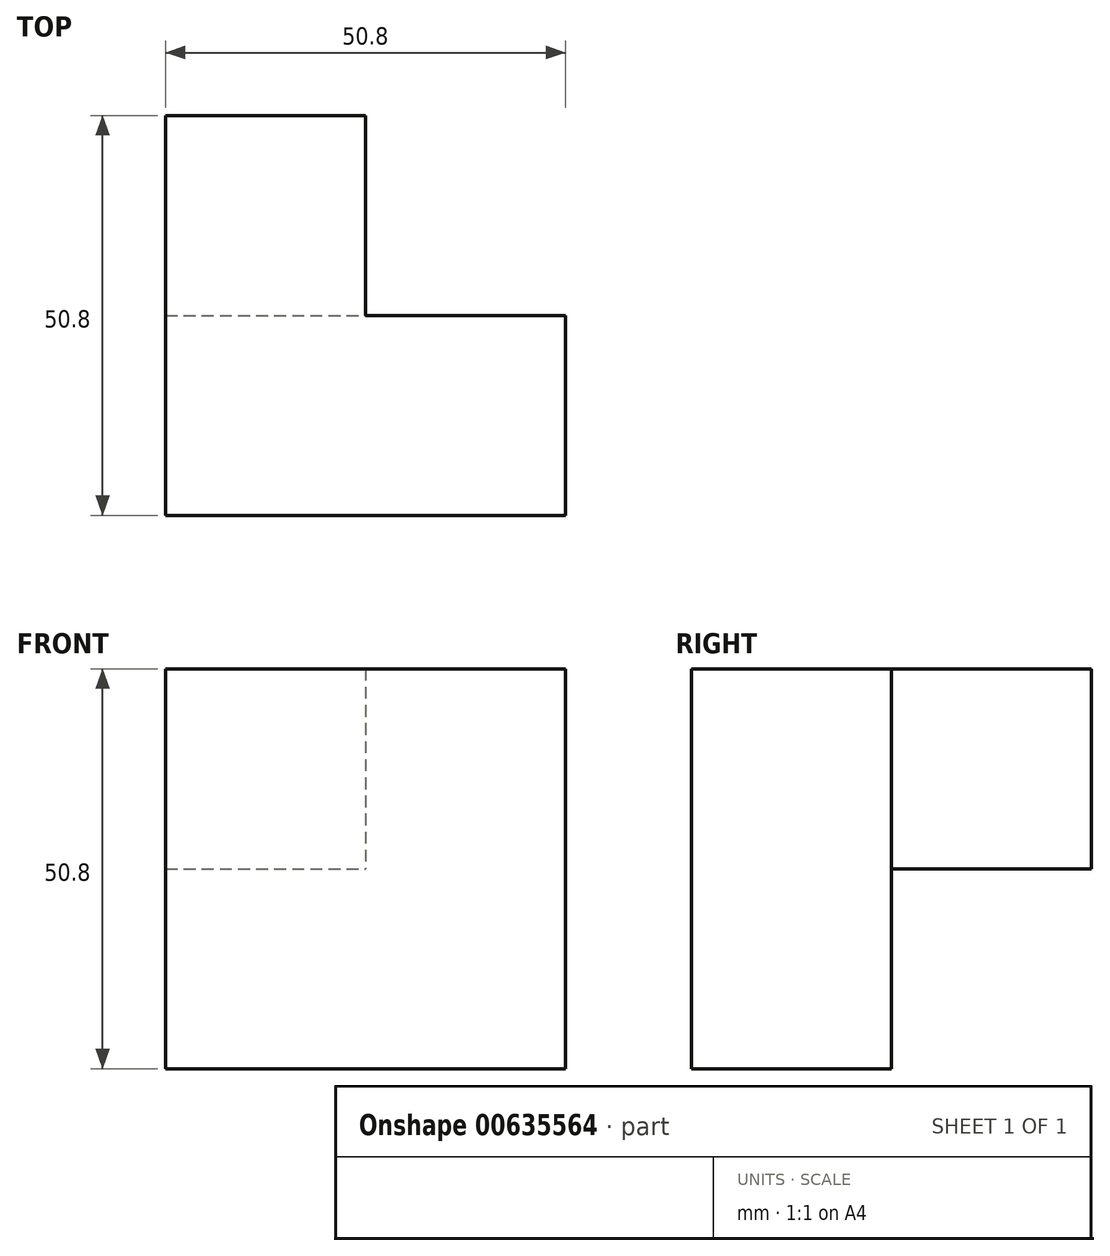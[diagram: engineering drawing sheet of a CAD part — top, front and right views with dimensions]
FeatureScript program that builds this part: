
annotation { "Feature Type Name" : "Feature", "Feature Type Description" : "" }
export const myFeature = defineFeature(function(context is Context, id is Id, definition is map)
    precondition{}
    {
        {
            var Q0;
            Q0=qCreatedBy(makeId("Top.planeOp"),FACE);
            var sketch = newSketch(context, id + "F0", { "sketchPlane" : qUnion([Q0])});
            skLineSegment(sketch, "E0.bottom", {"start": v(0, 0) * mm, "end": v(50.8, 0) * mm});
            skLineSegment(sketch, "E0.top", {"start": v(0, 25.4) * mm, "end": v(50.8, 25.4) * mm});
            skLineSegment(sketch, "E0.left", {"start": v(0, 0) * mm, "end": v(0, 25.4) * mm});
            skLineSegment(sketch, "E0.right", {"start": v(50.8, 0) * mm, "end": v(50.8, 25.4) * mm});
            skPoint(sketch, "E1.oppositeSnap0", {"position": v(25.4, 0) * mm});
            skLineSegment(sketch, "E1.bottom", {"start": v(0, 0) * mm, "end": v(25.4, 0) * mm});
            skLineSegment(sketch, "E1.top", {"start": v(0, 50.8) * mm, "end": v(25.4, 50.8) * mm});
            skLineSegment(sketch, "E1.left", {"start": v(0, 0) * mm, "end": v(0, 50.8) * mm});
            skLineSegment(sketch, "E1.right", {"start": v(25.4, 0) * mm, "end": v(25.4, 50.8) * mm});
            skSolve(sketch);
        }
        {
            var Q0;
            Q0 = qSketchRegion(id + "F0", true);
            extrude(context, id + "F1", {"entities" : qUnion([Q0]), "depth" : 50.8 * mm, "offsetDistance" : 25.4 * mm});
        }
        {
            var Q0;
            {var subQ5=sQuery(id+"F0.wireOp",EDGE,"E1.bottom");Q0=makeQuery(id+"F0.imprint","IMPRINT",FACE,{"disambiguationData":[TD([[makeQuery(id+"F0.imprint","IMPRINT",EDGE,{"derivedFrom":subQ5}),1.0]])]});}
            var Q1;
            {var subQ5=sQuery(id+"F0.wireOp",EDGE,"E1.top");Q1=makeQuery(id+"F0.imprint","IMPRINT",FACE,{"disambiguationData":[TD([[makeQuery(id+"F0.imprint","IMPRINT",EDGE,{"derivedFrom":subQ5}),-1.0]])]});}
            extrude(context, id + "F2", {"entities" : qUnion([Q0, Q1]), "operationType" : NewBodyOperationType.REMOVE, "depth" : 25.4 * mm, "offsetDistance" : 25.4 * mm});
        }
    });
